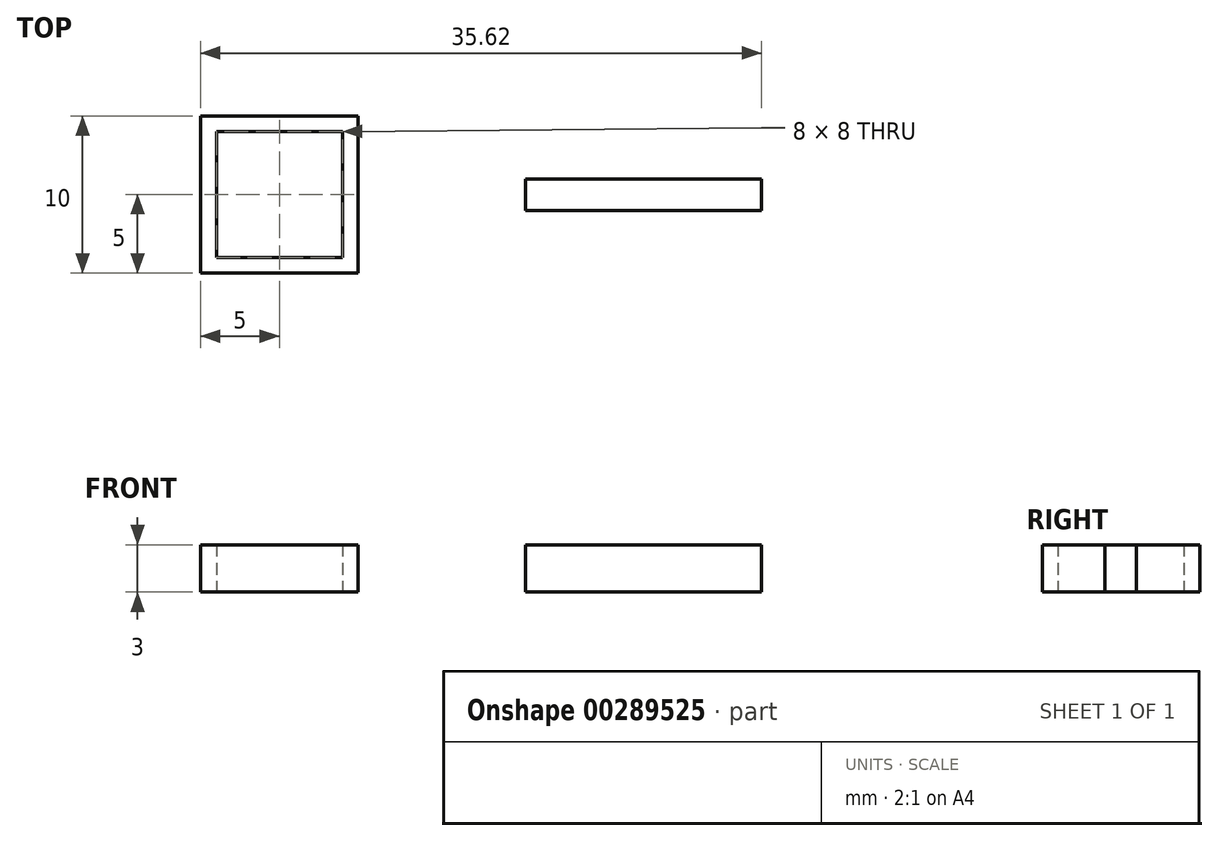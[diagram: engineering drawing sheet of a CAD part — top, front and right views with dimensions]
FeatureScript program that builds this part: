
annotation { "Feature Type Name" : "Feature", "Feature Type Description" : "" }
export const myFeature = defineFeature(function(context is Context, id is Id, definition is map)
    precondition{}
    {
        {
            var Q0;
            Q0=qCreatedBy(makeId("Top.planeOp"),FACE);
            var sketch = newSketch(context, id + "F0", { "sketchPlane" : qUnion([Q0])});
            skLineSegment(sketch, "E0.bottom", {"start": v(5, 5) * mm, "end": v(-5, 5) * mm});
            skLineSegment(sketch, "E0.top", {"start": v(5, -5) * mm, "end": v(-5, -5) * mm});
            skLineSegment(sketch, "E0.left", {"start": v(5, 5) * mm, "end": v(5, -5) * mm});
            skLineSegment(sketch, "E0.right", {"start": v(-5, 5) * mm, "end": v(-5, -5) * mm});
            skPoint(sketch, "E0.middle", {"position": v(0, 0) * mm});
            skLineSegment(sketch, "E1.bottom", {"start": v(4, 4) * mm, "end": v(-4, 4) * mm});
            skLineSegment(sketch, "E1.top", {"start": v(4, -4) * mm, "end": v(-4, -4) * mm});
            skLineSegment(sketch, "E1.left", {"start": v(4, 4) * mm, "end": v(4, -4) * mm});
            skLineSegment(sketch, "E1.right", {"start": v(-4, 4) * mm, "end": v(-4, -4) * mm});
            skLineSegment(sketch, "E2.bottom", {"start": v(15.62, 1) * mm, "end": v(30.62, 1) * mm});
            skLineSegment(sketch, "E2.top", {"start": v(15.62, -1) * mm, "end": v(30.62, -1) * mm});
            skLineSegment(sketch, "E2.left", {"start": v(15.62, 1) * mm, "end": v(15.62, -1) * mm});
            skLineSegment(sketch, "E2.right", {"start": v(30.62, 1) * mm, "end": v(30.62, -1) * mm});
            skPoint(sketch, "E2.middle", {"position": v(23.12, 0) * mm});
            skSolve(sketch);
        }
        {
            var Q0;
            Q0=makeQuery(id+"F0.imprint","IMPRINT",FACE,{"disambiguationData":[TD([[makeQuery(id+"F0.imprint","IMPRINT",EDGE,{"derivedFrom":sQuery(id+"F0.wireOp",EDGE,"E0.bottom")}),1.0]])]});
            extrude(context, id + "F1", {"entities" : qUnion([Q0]), "depth" : 2 * mm});
        }
        {
            var Q0;
            Q0 = qSketchRegion(id + "F0", true);
            extrude(context, id + "F2", {"entities" : qUnion([Q0]), "operationType" : NewBodyOperationType.ADD, "depth" : 3 * mm});
        }
    });
